# Revit family: 6L-W-D
name_source: partatom
category: Lighting Fixtures
revit_build: Autodesk Revit 2014 (Build: 20130308_1515(x64)
units: mm (PartAtom-declared; Revit-internal decimal feet)

## types (6) — shared parameters
Apparent Load = 0 VA
Assembly Code = D5020200
Color Filter = 16777215
Default Elevation = 48 "
Description = The MOD™ 6L LED Wall Direct (6L-W-D) is part of the MODx family, which is an affordably-priced, full-featured offering with best-in-class attention to detail.
Diming Protocol = 0-10V, Lutron 2-Wire, Lutron 3-Wire, Lutron Ecosystem Digital, Step-dimming
Dimming Lamp Color Temperature Shift = <None>
Emit Shape Visible in Rendering = No
Emit from Rectangle Length = 6 "
Fixture Distribution = Direct
Glass = Glass - Hubbell - White
Housing Material = Paint - Hubbell - Matte White
Lamp = LED
Load Classification = Lighting
Manufacturer = Litecontrol Lighting
Model = MOD™ 6L LED Wall Direct
Mounting = Wall-Mount
Photometric Notes = For more Photometric web files please find the photmetric web link
Photometric Web File = 6L-W-D-4-BAT-X-CX-35K-D030.ies
Photometric Web Link = https://www.hubbell.com
Power Factor = 1
Product Documentation Link = https://hubbellcdn.com
Product Page URL = https://www.hubbell.com
Tilt Angle = 90.00°
Type Comments = Lighting Fixture
URL = https://www.hubbell.com
Voltage = 120 V
Warranty = 5-Years Warranty

## per-type parameters (varying)
| type | Emit from Rectangle Width | zz Length 1 | zz YesNo 1 | zz YesNo 2 |
| 6L-W-D-02 | 24 " | 24 " | Yes | No |
| 6L-W-D-03 | 36 " | 36 " | No | Yes |
| 6L-W-D-04 | 48 " | 48 " | No | Yes |
| 6L-W-D-05 | 60 " | 60 " | No | Yes |
| 6L-W-D-06 | 72 " | 72 " | No | Yes |
| 6L-W-D-08 | 96 " | 96 " | No | Yes |

## geometry (parser evidence)
native form markers: Sweep x3
no freeform markers — native parametric forms only
